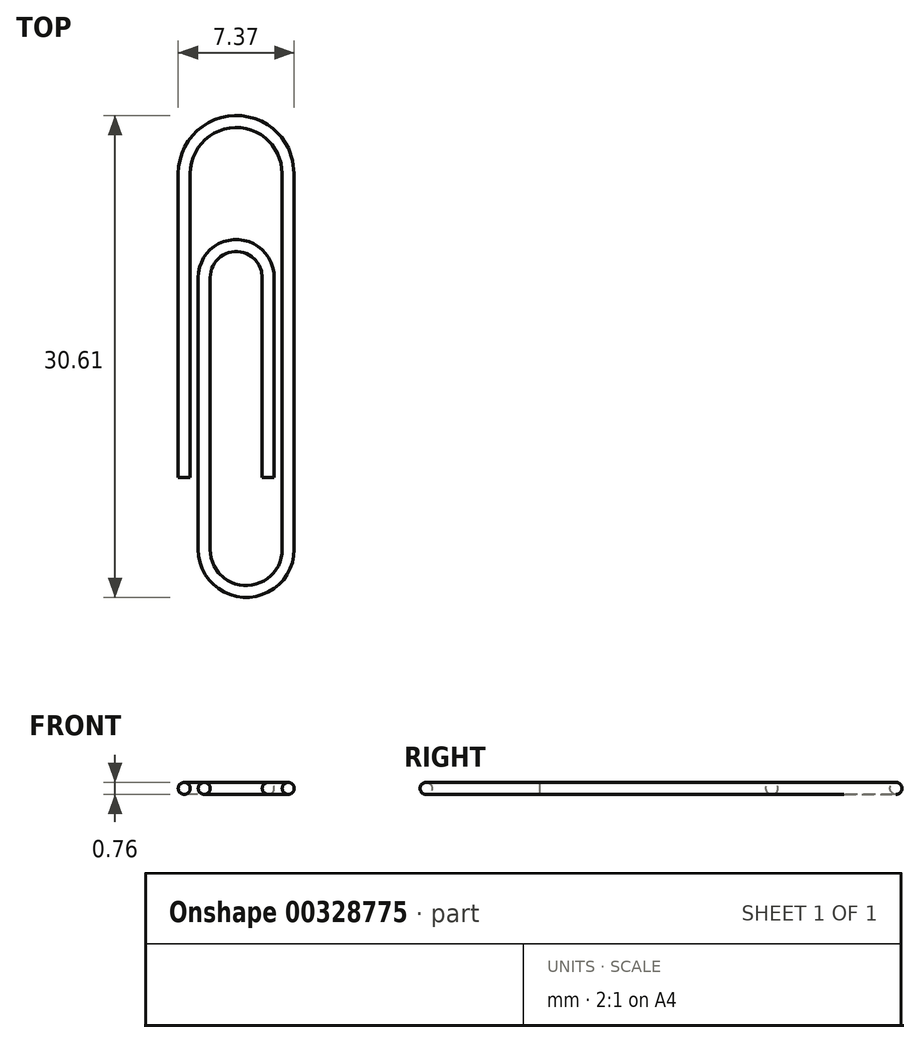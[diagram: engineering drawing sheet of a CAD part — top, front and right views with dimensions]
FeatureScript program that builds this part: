
annotation { "Feature Type Name" : "Feature", "Feature Type Description" : "" }
export const myFeature = defineFeature(function(context is Context, id is Id, definition is map)
    precondition{}
    {
        {
            var Q0;
            Q0=qCreatedBy(makeId("Top.planeOp"),FACE);
            var sketch = newSketch(context, id + "F0", { "sketchPlane" : qUnion([Q0])});
            skLineSegment(sketch, "E0", {"start": v(0, 0) * mm, "end": v(0, 12.7) * mm});
            skArc(sketch, "E1", {"start": v(0, 12.7) * mm, "mid": v(-2.03, 14.73) * mm, "end": v(-4.06, 12.7) * mm});
            skLineSegment(sketch, "E2", {"start": v(-4.06, 12.7) * mm, "end": v(-4.06, -4.57) * mm});
            skArc(sketch, "E3", {"start": v(-4.06, -4.57) * mm, "mid": v(-1.4, -7.24) * mm, "end": v(1.27, -4.57) * mm});
            skLineSegment(sketch, "E4", {"start": v(1.27, -4.57) * mm, "end": v(1.27, 19.3) * mm});
            skArc(sketch, "E5", {"start": v(1.27, 19.3) * mm, "mid": v(-2.03, 22.6) * mm, "end": v(-5.33, 19.3) * mm});
            skLineSegment(sketch, "E6", {"start": v(-5.33, 19.3) * mm, "end": v(-5.33, 0) * mm});
            skSolve(sketch);
        }
        {
            var Q0;
            Q0=qCreatedBy(makeId("Front.planeOp"),FACE);
            var sketch = newSketch(context, id + "F1", { "sketchPlane" : qUnion([Q0])});
            skCircle(sketch, "E7", {"center": v(0, 0) * mm, "radius": 0.38 * mm});
            skSolve(sketch);
        }
        {
            var Q0;
            Q0=makeQuery(id+"F1.imprint","IMPRINT",FACE,{"disambiguationData":[TD([[makeQuery(id+"F1.imprint","IMPRINT",EDGE,{"derivedFrom":sQuery(id+"F1.wireOp",EDGE,"E7")}),1.0]])]});
            var Q1;
            Q1=sQuery(id+"F0.wireOp",EDGE,"E0");
            var Q2;
            Q2=sQuery(id+"F0.wireOp",EDGE,"E1");
            var Q3;
            Q3=sQuery(id+"F0.wireOp",EDGE,"E2");
            var Q4;
            Q4=sQuery(id+"F0.wireOp",EDGE,"E3");
            var Q5;
            Q5=sQuery(id+"F0.wireOp",EDGE,"E4");
            var Q6;
            Q6=sQuery(id+"F0.wireOp",EDGE,"E5");
            var Q7;
            Q7=sQuery(id+"F0.wireOp",EDGE,"E6");
            sweep(context, id + "F2", {"profiles" : qUnion([Q0]), "path" : qUnion([Q1, Q2, Q3, Q4, Q5, Q6, Q7])});
        }
    });
